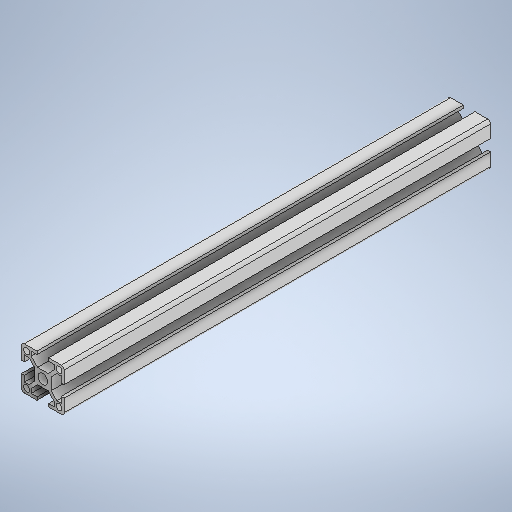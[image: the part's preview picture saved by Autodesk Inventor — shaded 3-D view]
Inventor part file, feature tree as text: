
AUTODESK INVENTOR PART (.ipt)
format: ipt  version: 2025 (Build 290162000, 162)  size: 310,272 bytes
history: native  units: in
note: dims shown in document units (in); Inventor stores cm internally (conversion verified against a paired STEP export)
features: extrude x1, sketch x1
ambient origin geometry x8: Origin, YZ Plane, XZ Plane, XY Plane, X Axis, Y Axis, Z Axis, Center Point
bodies: Solid1 (feature_tree)
feature tree (2):
  extrude  "Extrusion1"  Depth=11.811in
  sketch  "Sketch1"  dims[d6=11.811in d7=0.0in d8=0.1969in d9=0.0344in]
